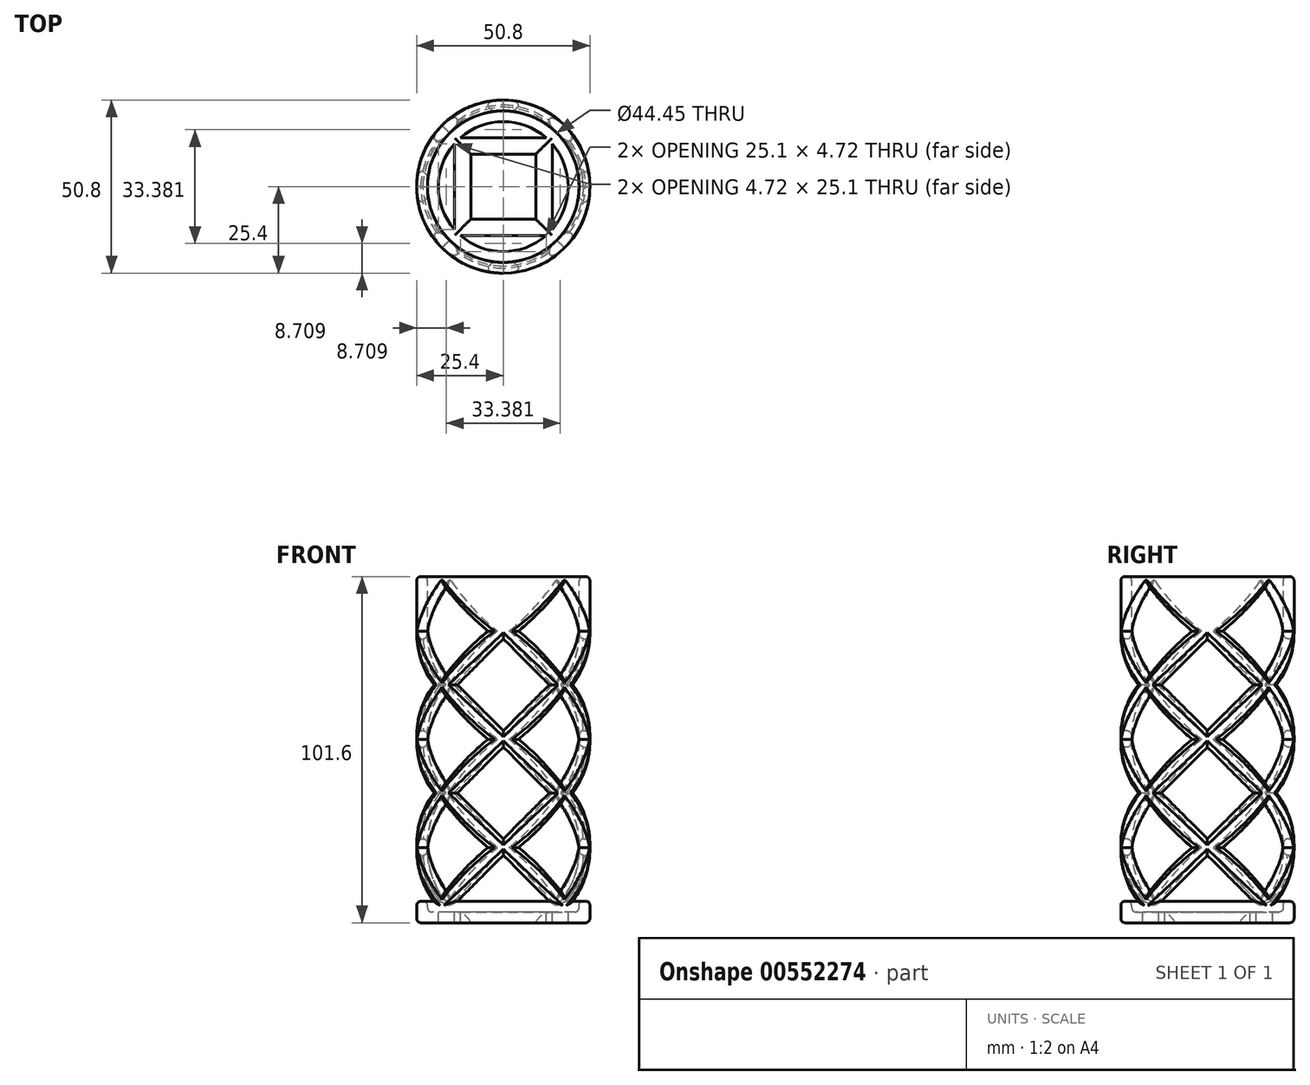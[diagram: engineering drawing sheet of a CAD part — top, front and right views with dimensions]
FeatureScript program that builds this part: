
annotation { "Feature Type Name" : "Feature", "Feature Type Description" : "" }
export const myFeature = defineFeature(function(context is Context, id is Id, definition is map)
    precondition{}
    {
        {
            var Q0;
            Q0=qCreatedBy(makeId("Top.planeOp"),FACE);
            var sketch = newSketch(context, id + "F0", { "sketchPlane" : qUnion([Q0])});
            skCircle(sketch, "E0", {"center": v(0, 0) * mm, "radius": 25.4 * mm});
            skSolve(sketch);
        }
        {
            var Q0;
            Q0=makeQuery(id+"F0.imprint","IMPRINT",FACE,{"disambiguationData":[TD([[makeQuery(id+"F0.imprint","IMPRINT",EDGE,{"derivedFrom":sQuery(id+"F0.wireOp",EDGE,"E0")}),1.0]])]});
            extrude(context, id + "F1", {"entities" : qUnion([Q0]), "depth" : 101.6 * mm, "offsetDistance" : 25.4 * mm});
        }
        {
            var Q0;
            Q0=qCreatedBy(makeId("Front.planeOp"),FACE);
            var sketch = newSketch(context, id + "F2", { "sketchPlane" : qUnion([Q0])});
            skLineSegment(sketch, "E1.0", {"start": v(-25.4, 0) * mm, "end": v(25.4, 0) * mm, "construction": true});
            skLineSegment(sketch, "E2", {"start": v(-25.4, 0) * mm, "end": v(-25.4, 101.6) * mm, "construction": true});
            skLineSegment(sketch, "E3.0", {"start": v(-25.4, 101.6) * mm, "end": v(25.4, 101.6) * mm, "construction": true});
            skLineSegment(sketch, "E4", {"start": v(25.4, 101.6) * mm, "end": v(25.4, 0) * mm, "construction": true});
            skLineSegment(sketch, "E5", {"start": v(0, 0) * mm, "end": v(0, 101.6) * mm, "construction": true});
            skCircle(sketch, "E6.cCircle", {"center": v(0, 133.35) * mm, "radius": 9.53 * mm, "construction": true});
            skLineSegment(sketch, "E6.0", {"start": v(0, 119.88) * mm, "end": v(-13.47, 133.35) * mm, "construction": true});
            skLineSegment(sketch, "E6.1", {"start": v(-13.47, 133.35) * mm, "end": v(0, 146.82) * mm, "construction": true});
            skLineSegment(sketch, "E6.2", {"start": v(0, 146.82) * mm, "end": v(13.47, 133.35) * mm, "construction": true});
            skLineSegment(sketch, "E6.3", {"start": v(13.47, 133.35) * mm, "end": v(0, 119.88) * mm, "construction": true});
            skLineSegment(sketch, "E7.0.1.0", {"start": v(0, 88.13) * mm, "end": v(-13.47, 101.6) * mm, "construction": true});
            skCircle(sketch, "E7.0.1.1", {"center": v(0, 101.6) * mm, "radius": 9.53 * mm, "construction": true});
            skLineSegment(sketch, "E7.0.1.2", {"start": v(-13.47, 101.6) * mm, "end": v(0, 115.07) * mm, "construction": true});
            skLineSegment(sketch, "E7.0.1.3", {"start": v(0, 115.07) * mm, "end": v(13.47, 101.6) * mm, "construction": true});
            skLineSegment(sketch, "E7.0.1.4", {"start": v(13.47, 101.6) * mm, "end": v(0, 88.13) * mm, "construction": true});
            skLineSegment(sketch, "E7.0.2.0", {"start": v(0, 56.38) * mm, "end": v(-13.47, 69.85) * mm});
            skCircle(sketch, "E7.0.2.1", {"center": v(0, 69.85) * mm, "radius": 9.53 * mm, "construction": true});
            skLineSegment(sketch, "E7.0.2.2", {"start": v(-13.47, 69.85) * mm, "end": v(0, 83.32) * mm});
            skLineSegment(sketch, "E7.0.2.3", {"start": v(0, 83.32) * mm, "end": v(13.47, 69.85) * mm});
            skLineSegment(sketch, "E7.0.2.4", {"start": v(13.47, 69.85) * mm, "end": v(0, 56.38) * mm});
            skLineSegment(sketch, "E7.0.3.0", {"start": v(0, 24.63) * mm, "end": v(-13.47, 38.1) * mm});
            skCircle(sketch, "E7.0.3.1", {"center": v(0, 38.1) * mm, "radius": 9.53 * mm, "construction": true});
            skLineSegment(sketch, "E7.0.3.2", {"start": v(-13.47, 38.1) * mm, "end": v(0, 51.57) * mm});
            skLineSegment(sketch, "E7.0.3.3", {"start": v(0, 51.57) * mm, "end": v(13.47, 38.1) * mm});
            skLineSegment(sketch, "E7.0.3.4", {"start": v(13.47, 38.1) * mm, "end": v(0, 24.63) * mm});
            skLineSegment(sketch, "E7.0.4.0", {"start": v(-6.74, -0.39) * mm, "end": v(-7.12, 0) * mm});
            skArc(sketch, "E7.0.4.1", {"start": v(-7.1, 0) * mm, "mid": v(-6.92, -0.2) * mm, "end": v(-6.74, -0.39) * mm, "construction": true});
            skLineSegment(sketch, "E7.0.4.2", {"start": v(-13.47, 6.35) * mm, "end": v(0, 19.82) * mm});
            skLineSegment(sketch, "E7.0.4.3", {"start": v(0, 19.82) * mm, "end": v(13.47, 6.35) * mm});
            skLineSegment(sketch, "E7.0.4.4", {"start": v(7.12, 0) * mm, "end": v(6.74, -0.39) * mm});
            skLineSegment(sketch, "E7.direction1", {"start": v(0, 119.88) * mm, "end": v(25.4, 119.88) * mm, "construction": true});
            skLineSegment(sketch, "E7.direction2", {"start": v(0, 119.88) * mm, "end": v(0, 88.13) * mm, "construction": true});
            skLineSegment(sketch, "E8", {"start": v(-13.47, 6.35) * mm, "end": v(13.47, 6.35) * mm});
            skArc(sketch, "E9.trimOffspring", {"start": v(6.74, -0.39) * mm, "mid": v(6.92, -0.2) * mm, "end": v(7.1, 0) * mm, "construction": true});
            skArc(sketch, "E10.trimOffspring", {"start": v(9.53, 6.35) * mm, "mid": v(0, 15.88) * mm, "end": v(-9.52, 6.35) * mm, "construction": true});
            skLineSegment(sketch, "E11", {"start": v(-25.4, 101.6) * mm, "end": v(0, 101.6) * mm, "construction": true});
            skLineSegment(sketch, "E12", {"start": v(25.4, 101.6) * mm, "end": v(0, 101.6) * mm, "construction": true});
            skSolve(sketch);
        }
        {
            var Q0;
            Q0=qSketchRegion(id+"F2",true);
            extrude(context, id + "F3", {"entities" : qUnion([Q0]), "operationType" : NewBodyOperationType.REMOVE, "endBound" : BoundingType.SYMMETRIC, "oppositeDirection" : true, "depth" : 50.8 * mm, "offsetDistance" : 25.4 * mm});
        }
        {
            var Q0;
            Q0=qCreatedBy(makeId("Right.planeOp"),FACE);
            var sketch = newSketch(context, id + "F4", { "sketchPlane" : qUnion([Q0])});
            skLineSegment(sketch, "E13.0", {"start": v(-25.4, 152.37) * mm, "end": v(25.4, 152.37) * mm, "construction": true});
            skLineSegment(sketch, "E14", {"start": v(0, -0.03) * mm, "end": v(0, 152.37) * mm, "construction": true});
            skLineSegment(sketch, "E15.0", {"start": v(-25.4, 152.4) * mm, "end": v(25.4, 152.4) * mm, "construction": true});
            skLineSegment(sketch, "E16", {"start": v(0, 0) * mm, "end": v(0, 152.4) * mm, "construction": true});
            skLineSegment(sketch, "E17", {"start": v(-25.4, 0) * mm, "end": v(-25.4, 152.4) * mm, "construction": true});
            skLineSegment(sketch, "E18", {"start": v(25.4, 152.4) * mm, "end": v(25.4, 0) * mm, "construction": true});
            skLineSegment(sketch, "E19", {"start": v(-25.4, 0) * mm, "end": v(25.4, 0) * mm, "construction": true});
            skCircle(sketch, "E20.cCircle", {"center": v(0, 133.35) * mm, "radius": 9.53 * mm, "construction": true});
            skLineSegment(sketch, "E20.0", {"start": v(0, 119.88) * mm, "end": v(-13.48, 133.35) * mm, "construction": true});
            skLineSegment(sketch, "E20.1", {"start": v(-13.48, 133.35) * mm, "end": v(0, 146.82) * mm, "construction": true});
            skLineSegment(sketch, "E20.2", {"start": v(0, 146.82) * mm, "end": v(13.46, 133.35) * mm, "construction": true});
            skLineSegment(sketch, "E20.3", {"start": v(13.46, 133.35) * mm, "end": v(0, 119.88) * mm, "construction": true});
            skLineSegment(sketch, "E21.0.1.0", {"start": v(0, 88.13) * mm, "end": v(-13.48, 101.6) * mm, "construction": true});
            skCircle(sketch, "E21.0.1.1", {"center": v(0, 101.6) * mm, "radius": 9.53 * mm, "construction": true});
            skLineSegment(sketch, "E21.0.1.2", {"start": v(-13.48, 101.6) * mm, "end": v(0, 115.07) * mm, "construction": true});
            skLineSegment(sketch, "E21.0.1.3", {"start": v(0, 115.07) * mm, "end": v(13.46, 101.6) * mm, "construction": true});
            skLineSegment(sketch, "E21.0.1.4", {"start": v(13.46, 101.6) * mm, "end": v(0, 88.13) * mm, "construction": true});
            skLineSegment(sketch, "E21.0.2.0", {"start": v(0, 56.38) * mm, "end": v(-13.48, 69.85) * mm});
            skCircle(sketch, "E21.0.2.1", {"center": v(0, 69.85) * mm, "radius": 9.53 * mm, "construction": true});
            skLineSegment(sketch, "E21.0.2.2", {"start": v(-13.48, 69.85) * mm, "end": v(0, 83.32) * mm});
            skLineSegment(sketch, "E21.0.2.3", {"start": v(0, 83.32) * mm, "end": v(13.46, 69.85) * mm});
            skLineSegment(sketch, "E21.0.2.4", {"start": v(13.46, 69.85) * mm, "end": v(0, 56.38) * mm});
            skLineSegment(sketch, "E21.0.3.0", {"start": v(0, 24.63) * mm, "end": v(-13.48, 38.1) * mm});
            skCircle(sketch, "E21.0.3.1", {"center": v(0, 38.1) * mm, "radius": 9.53 * mm, "construction": true});
            skLineSegment(sketch, "E21.0.3.2", {"start": v(-13.48, 38.1) * mm, "end": v(0, 51.57) * mm});
            skLineSegment(sketch, "E21.0.3.3", {"start": v(0, 51.57) * mm, "end": v(13.46, 38.1) * mm});
            skLineSegment(sketch, "E21.0.3.4", {"start": v(13.46, 38.1) * mm, "end": v(0, 24.63) * mm});
            skLineSegment(sketch, "E21.0.4.0", {"start": v(-6.74, -0.39) * mm, "end": v(-7.13, 0) * mm});
            skArc(sketch, "E21.0.4.1", {"start": v(-7.1, 0) * mm, "mid": v(-6.93, -0.2) * mm, "end": v(-6.74, -0.39) * mm, "construction": true});
            skLineSegment(sketch, "E21.0.4.2", {"start": v(-13.48, 6.35) * mm, "end": v(0, 19.82) * mm});
            skLineSegment(sketch, "E21.0.4.3", {"start": v(0, 19.82) * mm, "end": v(13.46, 6.35) * mm});
            skLineSegment(sketch, "E21.0.4.4", {"start": v(7.11, 0) * mm, "end": v(6.73, -0.39) * mm});
            skLineSegment(sketch, "E21.direction1", {"start": v(0, 119.88) * mm, "end": v(25.4, 119.88) * mm, "construction": true});
            skLineSegment(sketch, "E21.direction2", {"start": v(0, 119.88) * mm, "end": v(0, 88.13) * mm, "construction": true});
            skLineSegment(sketch, "E22", {"start": v(-13.48, 6.35) * mm, "end": v(13.46, 6.35) * mm});
            skArc(sketch, "E23.trimOffspring", {"start": v(6.73, -0.39) * mm, "mid": v(6.91, -0.2) * mm, "end": v(7.1, 0) * mm, "construction": true});
            skArc(sketch, "E24.trimOffspring", {"start": v(9.52, 6.35) * mm, "mid": v(0, 15.88) * mm, "end": v(-9.53, 6.35) * mm, "construction": true});
            skSolve(sketch);
        }
        {
            var Q0;
            Q0=qSketchRegion(id+"F4",true);
            var Q1;
            Q1=sQuery(id+"F4.wireOp",EDGE,"2f13abd6-07ff-4814-b25a-54ffae8c317d.5");
            var Q2;
            Q2=sQuery(id+"F4.wireOp",EDGE,"2f13abd6-07ff-4814-b25a-54ffae8c317d.4");
            var Q3;
            Q3=sQuery(id+"F4.wireOp",EDGE,"2f13abd6-07ff-4814-b25a-54ffae8c317d.0");
            var Q4;
            Q4=sQuery(id+"F4.wireOp",EDGE,"2f13abd6-07ff-4814-b25a-54ffae8c317d.3");
            var Q5;
            Q5=sQuery(id+"F4.wireOp",EDGE,"2f13abd6-07ff-4814-b25a-54ffae8c317d.2");
            var Q6;
            Q6=sQuery(id+"F4.wireOp",EDGE,"2f13abd6-07ff-4814-b25a-54ffae8c317d.1");
            var Q7;
            Q7=sQuery(id+"F4.wireOp",EDGE,"6f1e5377-79db-41f7-a9aa-e35f999cc832.0.1.7");
            var Q8;
            Q8=sQuery(id+"F4.wireOp",EDGE,"6f1e5377-79db-41f7-a9aa-e35f999cc832.0.1.4");
            var Q9;
            Q9=sQuery(id+"F4.wireOp",EDGE,"6f1e5377-79db-41f7-a9aa-e35f999cc832.0.1.1");
            var Q10;
            Q10=sQuery(id+"F4.wireOp",EDGE,"6f1e5377-79db-41f7-a9aa-e35f999cc832.0.1.2");
            var Q11;
            Q11=sQuery(id+"F4.wireOp",EDGE,"6f1e5377-79db-41f7-a9aa-e35f999cc832.0.1.0");
            var Q12;
            Q12=sQuery(id+"F4.wireOp",EDGE,"6f1e5377-79db-41f7-a9aa-e35f999cc832.0.1.6");
            var Q13;
            Q13=sQuery(id+"F4.wireOp",EDGE,"6f1e5377-79db-41f7-a9aa-e35f999cc832.0.2.2");
            var Q14;
            Q14=sQuery(id+"F4.wireOp",EDGE,"6f1e5377-79db-41f7-a9aa-e35f999cc832.0.2.1");
            var Q15;
            Q15=sQuery(id+"F4.wireOp",EDGE,"6f1e5377-79db-41f7-a9aa-e35f999cc832.0.2.4");
            var Q16;
            Q16=sQuery(id+"F4.wireOp",EDGE,"6f1e5377-79db-41f7-a9aa-e35f999cc832.0.2.7");
            var Q17;
            Q17=sQuery(id+"F4.wireOp",EDGE,"6f1e5377-79db-41f7-a9aa-e35f999cc832.0.2.6");
            var Q18;
            Q18=sQuery(id+"F4.wireOp",EDGE,"6f1e5377-79db-41f7-a9aa-e35f999cc832.0.2.0");
            var Q19;
            Q19=sQuery(id+"F4.wireOp",EDGE,"6f1e5377-79db-41f7-a9aa-e35f999cc832.0.3.4");
            var Q20;
            Q20=sQuery(id+"F4.wireOp",EDGE,"6f1e5377-79db-41f7-a9aa-e35f999cc832.0.3.2");
            var Q21;
            Q21=sQuery(id+"F4.wireOp",EDGE,"6f1e5377-79db-41f7-a9aa-e35f999cc832.0.3.1");
            var Q22;
            Q22=sQuery(id+"F4.wireOp",EDGE,"6f1e5377-79db-41f7-a9aa-e35f999cc832.0.3.7");
            var Q23;
            Q23=sQuery(id+"F4.wireOp",EDGE,"6f1e5377-79db-41f7-a9aa-e35f999cc832.0.3.6");
            var Q24;
            Q24=sQuery(id+"F4.wireOp",EDGE,"6f1e5377-79db-41f7-a9aa-e35f999cc832.0.3.0");
            var Q25;
            Q25=sQuery(id+"F4.wireOp",EDGE,"6f1e5377-79db-41f7-a9aa-e35f999cc832.0.4.4");
            var Q26;
            Q26=sQuery(id+"F4.wireOp",EDGE,"6f1e5377-79db-41f7-a9aa-e35f999cc832.0.4.1");
            var Q27;
            Q27=sQuery(id+"F4.wireOp",EDGE,"6f1e5377-79db-41f7-a9aa-e35f999cc832.0.4.2");
            var Q28;
            Q28=sQuery(id+"F4.wireOp",EDGE,"6f1e5377-79db-41f7-a9aa-e35f999cc832.0.4.0");
            var Q29;
            Q29=sQuery(id+"F4.wireOp",EDGE,"6f1e5377-79db-41f7-a9aa-e35f999cc832.0.4.6");
            var Q30;
            Q30=sQuery(id+"F4.wireOp",EDGE,"6f1e5377-79db-41f7-a9aa-e35f999cc832.0.4.7");
            var Q31;
            Q31=sQuery(id+"F4.wireOp",EDGE,"6f1e5377-79db-41f7-a9aa-e35f999cc832.0.5.4");
            var Q32;
            Q32=sQuery(id+"F4.wireOp",EDGE,"6f1e5377-79db-41f7-a9aa-e35f999cc832.0.5.7");
            var Q33;
            Q33=sQuery(id+"F4.wireOp",EDGE,"6f1e5377-79db-41f7-a9aa-e35f999cc832.0.5.6");
            var Q34;
            Q34=sQuery(id+"F4.wireOp",EDGE,"6f1e5377-79db-41f7-a9aa-e35f999cc832.0.5.0");
            var Q35;
            Q35=sQuery(id+"F4.wireOp",EDGE,"6f1e5377-79db-41f7-a9aa-e35f999cc832.0.5.2");
            var Q36;
            Q36=sQuery(id+"F4.wireOp",EDGE,"6f1e5377-79db-41f7-a9aa-e35f999cc832.0.5.1");
            extrude(context, id + "F5", {"entities" : qUnion([Q0]), "operationType" : NewBodyOperationType.REMOVE, "surfaceEntities" : qUnion([Q1, Q2, Q3, Q4, Q5, Q6, Q7, Q8, Q9, Q10, Q11, Q12, Q13, Q14, Q15, Q16, Q17, Q18, Q19, Q20, Q21, Q22, Q23, Q24, Q25, Q26, Q27, Q28, Q29, Q30, Q31, Q32, Q33, Q34, Q35, Q36]), "endBound" : BoundingType.SYMMETRIC, "oppositeDirection" : true, "depth" : 50.8 * mm, "offsetDistance" : 25.4 * mm});
        }
        {
            var Q0;
            Q0=makeQuery(id+"F1.opExtrude","SWEPT_FACE",FACE,{"disambiguationData":[OSD([sQuery(id+"F0.wireOp",EDGE,"E0")])]});
            cPlane(context, id + "F6", {"entities" : qUnion([Q0]), "cplaneType" : CPlaneType.LINE_ANGLE, "offset" : 25.4 * mm, "angle" : 45 * degree, "oppositeDirection" : true, "width" : 152.4 * mm, "height" : 152.4 * mm});
        }
        {
            var Q0;
            Q0=qCreatedBy(id+"F6.planeOp",FACE);
            var sketch = newSketch(context, id + "F7", { "sketchPlane" : qUnion([Q0])});
            skLineSegment(sketch, "E25.0", {"start": v(-25.4, 101.6) * mm, "end": v(25.4, 101.6) * mm, "construction": true});
            skLineSegment(sketch, "E26", {"start": v(25.4, 152.4) * mm, "end": v(25.4, 0) * mm, "construction": true});
            skLineSegment(sketch, "E27", {"start": v(-25.4, 0) * mm, "end": v(-25.4, 152.4) * mm, "construction": true});
            skLineSegment(sketch, "E28.0", {"start": v(-25.4, 0) * mm, "end": v(25.4, 0) * mm, "construction": true});
            skLineSegment(sketch, "E29", {"start": v(0, 0) * mm, "end": v(0, 101.6) * mm, "construction": true});
            skPoint(sketch, "E30.0", {"position": v(17.96, 88.14) * mm});
            skPoint(sketch, "E31.0", {"position": v(17.96, 83.31) * mm});
            skLineSegment(sketch, "E32", {"start": v(17.96, 83.31) * mm, "end": v(17.96, 88.14) * mm, "construction": true});
            skLineSegment(sketch, "E33", {"start": v(17.96, 85.72) * mm, "end": v(-25.4, 85.72) * mm, "construction": true});
            skCircle(sketch, "E34.cCircle", {"center": v(0, 117.35) * mm, "radius": 9.53 * mm, "construction": true});
            skLineSegment(sketch, "E34.0", {"start": v(0, 103.88) * mm, "end": v(-13.47, 117.35) * mm});
            skLineSegment(sketch, "E34.1", {"start": v(-13.47, 117.35) * mm, "end": v(0, 130.82) * mm});
            skLineSegment(sketch, "E34.2", {"start": v(0, 130.82) * mm, "end": v(13.47, 117.35) * mm});
            skLineSegment(sketch, "E34.3", {"start": v(13.47, 117.35) * mm, "end": v(0, 103.88) * mm});
            skLineSegment(sketch, "E35.0.1.0", {"start": v(0, 72.13) * mm, "end": v(-13.47, 85.6) * mm});
            skCircle(sketch, "E35.0.1.1", {"center": v(0, 85.6) * mm, "radius": 9.53 * mm, "construction": true});
            skLineSegment(sketch, "E35.0.1.2", {"start": v(-13.47, 85.6) * mm, "end": v(0, 99.07) * mm});
            skLineSegment(sketch, "E35.0.1.3", {"start": v(0, 99.07) * mm, "end": v(13.47, 85.6) * mm});
            skLineSegment(sketch, "E35.0.1.4", {"start": v(13.47, 85.6) * mm, "end": v(0, 72.13) * mm});
            skLineSegment(sketch, "E35.0.2.0", {"start": v(0, 40.38) * mm, "end": v(-13.47, 53.85) * mm});
            skCircle(sketch, "E35.0.2.1", {"center": v(0, 53.85) * mm, "radius": 9.53 * mm, "construction": true});
            skLineSegment(sketch, "E35.0.2.2", {"start": v(-13.47, 53.85) * mm, "end": v(0, 67.32) * mm});
            skLineSegment(sketch, "E35.0.2.3", {"start": v(0, 67.32) * mm, "end": v(13.47, 53.85) * mm});
            skLineSegment(sketch, "E35.0.2.4", {"start": v(13.47, 53.85) * mm, "end": v(0, 40.38) * mm});
            skLineSegment(sketch, "E35.0.3.0", {"start": v(0, 8.63) * mm, "end": v(-13.47, 22.1) * mm});
            skCircle(sketch, "E35.0.3.1", {"center": v(0, 22.1) * mm, "radius": 9.53 * mm, "construction": true});
            skLineSegment(sketch, "E35.0.3.2", {"start": v(-13.47, 22.1) * mm, "end": v(0, 35.57) * mm});
            skLineSegment(sketch, "E35.0.3.3", {"start": v(0, 35.57) * mm, "end": v(13.47, 22.1) * mm});
            skLineSegment(sketch, "E35.0.3.4", {"start": v(13.47, 22.1) * mm, "end": v(0, 8.63) * mm});
            skLineSegment(sketch, "E35.direction1", {"start": v(0, 103.88) * mm, "end": v(25.4, 103.88) * mm, "construction": true});
            skLineSegment(sketch, "E35.direction2", {"start": v(0, 103.88) * mm, "end": v(0, 72.13) * mm, "construction": true});
            skSolve(sketch);
        }
        {
            var Q0;
            Q0=qSketchRegion(id+"F7",true);
            extrude(context, id + "F8", {"entities" : qUnion([Q0]), "operationType" : NewBodyOperationType.REMOVE, "endBound" : BoundingType.SYMMETRIC, "oppositeDirection" : true, "depth" : 50.8 * mm, "offsetDistance" : 25.4 * mm});
        }
        {
            var Q0;
            Q0=makeQuery(id+"F1.opExtrude","SWEPT_FACE",FACE,{"disambiguationData":[OSD([sQuery(id+"F0.wireOp",EDGE,"E0")])]});
            cPlane(context, id + "F9", {"entities" : qUnion([Q0]), "cplaneType" : CPlaneType.LINE_ANGLE, "offset" : 25.4 * mm, "angle" : 45 * degree, "width" : 152.4 * mm, "height" : 152.4 * mm});
        }
        {
            var Q0;
            Q0=qCreatedBy(id+"F9.planeOp",FACE);
            var sketch = newSketch(context, id + "F10", { "sketchPlane" : qUnion([Q0])});
            skLineSegment(sketch, "E36.0", {"start": v(-25.4, 0) * mm, "end": v(25.4, 0) * mm, "construction": true});
            skLineSegment(sketch, "E37.0", {"start": v(-25.4, 101.6) * mm, "end": v(25.4, 101.6) * mm, "construction": true});
            skLineSegment(sketch, "E38", {"start": v(25.4, 152.4) * mm, "end": v(25.4, 0) * mm, "construction": true});
            skLineSegment(sketch, "E39", {"start": v(-25.4, 0) * mm, "end": v(-25.4, 152.4) * mm, "construction": true});
            skLineSegment(sketch, "E40", {"start": v(0, 0) * mm, "end": v(0, 101.6) * mm, "construction": true});
            skLineSegment(sketch, "E41.0", {"start": v(-25.4, 152.4) * mm, "end": v(25.4, 152.4) * mm, "construction": true});
            skLineSegment(sketch, "E42", {"start": v(0, 0) * mm, "end": v(0, 152.4) * mm, "construction": true});
            skPoint(sketch, "E43.0", {"position": v(17.96, 88.14) * mm});
            skPoint(sketch, "E44.0", {"position": v(17.96, 83.31) * mm});
            skLineSegment(sketch, "E45", {"start": v(17.96, 83.31) * mm, "end": v(17.96, 88.14) * mm, "construction": true});
            skLineSegment(sketch, "E46", {"start": v(17.96, 85.72) * mm, "end": v(-25.4, 85.72) * mm, "construction": true});
            skCircle(sketch, "E47.cCircle", {"center": v(0, 117.35) * mm, "radius": 9.53 * mm, "construction": true});
            skLineSegment(sketch, "E47.0", {"start": v(0, 103.88) * mm, "end": v(-13.47, 117.35) * mm});
            skLineSegment(sketch, "E47.1", {"start": v(-13.47, 117.35) * mm, "end": v(0, 130.82) * mm});
            skLineSegment(sketch, "E47.2", {"start": v(0, 130.82) * mm, "end": v(13.47, 117.35) * mm});
            skLineSegment(sketch, "E47.3", {"start": v(13.47, 117.35) * mm, "end": v(0, 103.88) * mm});
            skLineSegment(sketch, "E48.0.1.0", {"start": v(0, 72.13) * mm, "end": v(-13.47, 85.6) * mm});
            skCircle(sketch, "E48.0.1.1", {"center": v(0, 85.6) * mm, "radius": 9.53 * mm, "construction": true});
            skLineSegment(sketch, "E48.0.1.2", {"start": v(-13.47, 85.6) * mm, "end": v(0, 99.07) * mm});
            skLineSegment(sketch, "E48.0.1.3", {"start": v(0, 99.07) * mm, "end": v(13.47, 85.6) * mm});
            skLineSegment(sketch, "E48.0.1.4", {"start": v(13.47, 85.6) * mm, "end": v(0, 72.13) * mm});
            skLineSegment(sketch, "E48.0.2.0", {"start": v(0, 40.38) * mm, "end": v(-13.47, 53.85) * mm});
            skCircle(sketch, "E48.0.2.1", {"center": v(0, 53.85) * mm, "radius": 9.53 * mm, "construction": true});
            skLineSegment(sketch, "E48.0.2.2", {"start": v(-13.47, 53.85) * mm, "end": v(0, 67.32) * mm});
            skLineSegment(sketch, "E48.0.2.3", {"start": v(0, 67.32) * mm, "end": v(13.47, 53.85) * mm});
            skLineSegment(sketch, "E48.0.2.4", {"start": v(13.47, 53.85) * mm, "end": v(0, 40.38) * mm});
            skLineSegment(sketch, "E48.0.3.0", {"start": v(0, 8.63) * mm, "end": v(-13.47, 22.1) * mm});
            skCircle(sketch, "E48.0.3.1", {"center": v(0, 22.1) * mm, "radius": 9.53 * mm, "construction": true});
            skLineSegment(sketch, "E48.0.3.2", {"start": v(-13.47, 22.1) * mm, "end": v(0, 35.57) * mm});
            skLineSegment(sketch, "E48.0.3.3", {"start": v(0, 35.57) * mm, "end": v(13.47, 22.1) * mm});
            skLineSegment(sketch, "E48.0.3.4", {"start": v(13.47, 22.1) * mm, "end": v(0, 8.63) * mm});
            skLineSegment(sketch, "E48.direction1", {"start": v(0, 103.88) * mm, "end": v(25.4, 103.88) * mm, "construction": true});
            skLineSegment(sketch, "E48.direction2", {"start": v(0, 103.88) * mm, "end": v(0, 72.13) * mm, "construction": true});
            skSolve(sketch);
        }
        {
            var Q0;
            Q0=qSketchRegion(id+"F10",true);
            extrude(context, id + "F11", {"entities" : qUnion([Q0]), "operationType" : NewBodyOperationType.REMOVE, "endBound" : BoundingType.SYMMETRIC, "oppositeDirection" : true, "depth" : 50.8 * mm, "offsetDistance" : 25.4 * mm});
        }
        {
            var Q0;
            Q0=makeQuery(id+"F1.opExtrude","CAP_FACE",FACE,{"disambiguationData":[OSD([sQuery(id+"F0.wireOp",EDGE,"E0")])],"isStart":false});
            var sketch = newSketch(context, id + "F12", { "sketchPlane" : qUnion([Q0])});
            skCircle(sketch, "E49", {"center": v(0, 0) * mm, "radius": 22.23 * mm});
            skCircle(sketch, "E50.cCircle", {"center": v(0, 0) * mm, "radius": 9.53 * mm, "construction": true});
            skLineSegment(sketch, "E50.0", {"start": v(9.52, -9.53) * mm, "end": v(-9.52, -9.53) * mm});
            skLineSegment(sketch, "E50.1", {"start": v(-9.52, -9.53) * mm, "end": v(-9.53, 9.53) * mm});
            skLineSegment(sketch, "E50.2", {"start": v(-9.53, 9.53) * mm, "end": v(9.53, 9.53) * mm});
            skLineSegment(sketch, "E50.3", {"start": v(9.53, 9.52) * mm, "end": v(9.53, -9.53) * mm});
            skPoint(sketch, "E50.0.midPoint", {"position": v(0, -9.53) * mm});
            skCircle(sketch, "E51", {"center": v(0, 0) * mm, "radius": 19.05 * mm});
            skLineSegment(sketch, "E52", {"start": v(-14.33, 12.55) * mm, "end": v(-14.33, -12.55) * mm});
            skLineSegment(sketch, "E53", {"start": v(-12.55, -14.33) * mm, "end": v(12.55, -14.33) * mm});
            skLineSegment(sketch, "E54", {"start": v(14.33, -12.55) * mm, "end": v(14.33, 12.55) * mm});
            skLineSegment(sketch, "E55", {"start": v(12.55, 14.33) * mm, "end": v(-12.55, 14.33) * mm});
            skSolve(sketch);
        }
        {
            var Q0;
            Q0=makeQuery(id+"F12.imprint","IMPRINT",FACE,{"disambiguationData":[TD([[makeQuery(id+"F12.imprint","IMPRINT",EDGE,{"derivedFrom":sQuery(id+"F12.wireOp",EDGE,"E50.0")}),-1.0]])]});
            var Q1;
            {var subQ0=sQuery(id+"F12.wireOp",EDGE,"6df1d413-d965-45c5-9bc1-fe74c4bacd03.1.5");Q1=makeQuery(id+"F12.imprint","IMPRINT",FACE,{"disambiguationData":[TD([[makeQuery(id+"F12.imprint","IMPRINT",EDGE,{"derivedFrom":subQ0}),-1.0]])]});}
            var Q2;
            {var subQ0=sQuery(id+"F12.wireOp",EDGE,"6df1d413-d965-45c5-9bc1-fe74c4bacd03.1.5");Q2=makeQuery(id+"F12.imprint","IMPRINT",FACE,{"disambiguationData":[TD([[makeQuery(id+"F12.imprint","IMPRINT",EDGE,{"derivedFrom":subQ0}),-1.0]])]});}
            var Q3;
            {var subQ0=sQuery(id+"F12.wireOp",EDGE,"1db86502-511d-4738-918a-1fb412958f63.1.0.2");Q3=makeQuery(id+"F12.imprint","IMPRINT",FACE,{"disambiguationData":[TD([[makeQuery(id+"F12.imprint","IMPRINT",EDGE,{"derivedFrom":subQ0}),-1.0]])]});}
            var Q4;
            {var subQ0=sQuery(id+"F12.wireOp",EDGE,"6df1d413-d965-45c5-9bc1-fe74c4bacd03.3.5");Q4=makeQuery(id+"F12.imprint","IMPRINT",FACE,{"disambiguationData":[TD([[makeQuery(id+"F12.imprint","IMPRINT",EDGE,{"derivedFrom":subQ0}),-1.0]])]});}
            var Q5;
            {var subQ0=sQuery(id+"F12.wireOp",EDGE,"6df1d413-d965-45c5-9bc1-fe74c4bacd03.2.5");Q5=makeQuery(id+"F12.imprint","IMPRINT",FACE,{"disambiguationData":[TD([[makeQuery(id+"F12.imprint","IMPRINT",EDGE,{"derivedFrom":subQ0}),-1.0]])]});}
            var Q6;
            {var subQ0=sQuery(id+"F12.wireOp",EDGE,"RcPyOSS5-Rkkl-329T-9cvf-4NeGbcBbp6hW.bottom");Q6=makeQuery(id+"F12.imprint","IMPRINT",FACE,{"disambiguationData":[TD([[makeQuery(id+"F12.imprint","IMPRINT",EDGE,{"derivedFrom":subQ0}),-1.0]])]});}
            var Q7;
            {var subQ0=sQuery(id+"F12.wireOp",EDGE,"RcPyOSS5-Rkkl-329T-9cvf-4NeGbcBbp6hW.right");Q7=makeQuery(id+"F12.imprint","IMPRINT",FACE,{"disambiguationData":[TD([[makeQuery(id+"F12.imprint","IMPRINT",EDGE,{"derivedFrom":subQ0}),-1.0]])]});}
            var Q8;
            {var subQ0=sQuery(id+"F12.wireOp",EDGE,"RcPyOSS5-Rkkl-329T-9cvf-4NeGbcBbp6hW.left");Q8=makeQuery(id+"F12.imprint","IMPRINT",FACE,{"disambiguationData":[TD([[makeQuery(id+"F12.imprint","IMPRINT",EDGE,{"derivedFrom":subQ0}),1.0]])]});}
            var Q9;
            {var subQ0=sQuery(id+"F12.wireOp",EDGE,"RcPyOSS5-Rkkl-329T-9cvf-4NeGbcBbp6hW.top");Q9=makeQuery(id+"F12.imprint","IMPRINT",FACE,{"disambiguationData":[TD([[makeQuery(id+"F12.imprint","IMPRINT",EDGE,{"derivedFrom":subQ0}),1.0]])]});}
            var Q10;
            {var subQ0=sQuery(id+"F12.wireOp",EDGE,"E52");Q10=makeQuery(id+"F12.imprint","IMPRINT",FACE,{"disambiguationData":[TD([[makeQuery(id+"F12.imprint","IMPRINT",EDGE,{"derivedFrom":subQ0}),-1.0]])]});}
            var Q11;
            {var subQ0=sQuery(id+"F12.wireOp",EDGE,"E55");Q11=makeQuery(id+"F12.imprint","IMPRINT",FACE,{"disambiguationData":[TD([[makeQuery(id+"F12.imprint","IMPRINT",EDGE,{"derivedFrom":subQ0}),-1.0]])]});}
            var Q12;
            {var subQ0=sQuery(id+"F12.wireOp",EDGE,"E54");Q12=makeQuery(id+"F12.imprint","IMPRINT",FACE,{"disambiguationData":[TD([[makeQuery(id+"F12.imprint","IMPRINT",EDGE,{"derivedFrom":subQ0}),-1.0]])]});}
            var Q13;
            {var subQ0=sQuery(id+"F12.wireOp",EDGE,"E53");Q13=makeQuery(id+"F12.imprint","IMPRINT",FACE,{"disambiguationData":[TD([[makeQuery(id+"F12.imprint","IMPRINT",EDGE,{"derivedFrom":subQ0}),-1.0]])]});}
            var Q14;
            Q14=makeQuery(id+"F12.imprint","IMPRINT",FACE,{"disambiguationData":[TD([[makeQuery(id+"F12.imprint","IMPRINT",EDGE,{"derivedFrom":sQuery(id+"F12.wireOp",EDGE,"E50.0")}),1.0]])]});
            var Q15;
            Q15=makeQuery(id+"F12.imprint","IMPRINT",FACE,{"disambiguationData":[TD([[makeQuery(id+"F12.imprint","IMPRINT",EDGE,{"derivedFrom":sQuery(id+"F12.wireOp",EDGE,"E49")}),1.0]])]});
            extrude(context, id + "F13", {"entities" : qUnion([Q0, Q1, Q2, Q3, Q4, Q5, Q6, Q7, Q8, Q9, Q10, Q11, Q12, Q13, Q14, Q15]), "operationType" : NewBodyOperationType.REMOVE, "oppositeDirection" : true, "depth" : 98.45 * mm, "offsetDistance" : 25.4 * mm});
        }
        {
            var Q0;
            {var subQ0=sQuery(id+"F12.wireOp",EDGE,"6df1d413-d965-45c5-9bc1-fe74c4bacd03.2.5");Q0=makeQuery(id+"F12.imprint","IMPRINT",FACE,{"disambiguationData":[TD([[makeQuery(id+"F12.imprint","IMPRINT",EDGE,{"derivedFrom":subQ0}),-1.0]])]});}
            var Q1;
            Q1=makeQuery(id+"F12.imprint","IMPRINT",FACE,{"disambiguationData":[TD([[makeQuery(id+"F12.imprint","IMPRINT",EDGE,{"derivedFrom":sQuery(id+"F12.wireOp",EDGE,"E50.0")}),-1.0]])]});
            var Q2;
            {var subQ0=sQuery(id+"F12.wireOp",EDGE,"6df1d413-d965-45c5-9bc1-fe74c4bacd03.1.5");Q2=makeQuery(id+"F12.imprint","IMPRINT",FACE,{"disambiguationData":[TD([[makeQuery(id+"F12.imprint","IMPRINT",EDGE,{"derivedFrom":subQ0}),-1.0]])]});}
            var Q3;
            {var subQ0=sQuery(id+"F12.wireOp",EDGE,"1db86502-511d-4738-918a-1fb412958f63.1.0.2");Q3=makeQuery(id+"F12.imprint","IMPRINT",FACE,{"disambiguationData":[TD([[makeQuery(id+"F12.imprint","IMPRINT",EDGE,{"derivedFrom":subQ0}),-1.0]])]});}
            var Q4;
            {var subQ0=sQuery(id+"F12.wireOp",EDGE,"6df1d413-d965-45c5-9bc1-fe74c4bacd03.3.5");Q4=makeQuery(id+"F12.imprint","IMPRINT",FACE,{"disambiguationData":[TD([[makeQuery(id+"F12.imprint","IMPRINT",EDGE,{"derivedFrom":subQ0}),-1.0]])]});}
            var Q5;
            {var subQ0=sQuery(id+"F12.wireOp",EDGE,"RcPyOSS5-Rkkl-329T-9cvf-4NeGbcBbp6hW.bottom");Q5=makeQuery(id+"F12.imprint","IMPRINT",FACE,{"disambiguationData":[TD([[makeQuery(id+"F12.imprint","IMPRINT",EDGE,{"derivedFrom":subQ0}),-1.0]])]});}
            var Q6;
            {var subQ0=sQuery(id+"F12.wireOp",EDGE,"RcPyOSS5-Rkkl-329T-9cvf-4NeGbcBbp6hW.right");Q6=makeQuery(id+"F12.imprint","IMPRINT",FACE,{"disambiguationData":[TD([[makeQuery(id+"F12.imprint","IMPRINT",EDGE,{"derivedFrom":subQ0}),-1.0]])]});}
            var Q7;
            {var subQ0=sQuery(id+"F12.wireOp",EDGE,"RcPyOSS5-Rkkl-329T-9cvf-4NeGbcBbp6hW.left");Q7=makeQuery(id+"F12.imprint","IMPRINT",FACE,{"disambiguationData":[TD([[makeQuery(id+"F12.imprint","IMPRINT",EDGE,{"derivedFrom":subQ0}),1.0]])]});}
            var Q8;
            {var subQ0=sQuery(id+"F12.wireOp",EDGE,"RcPyOSS5-Rkkl-329T-9cvf-4NeGbcBbp6hW.top");Q8=makeQuery(id+"F12.imprint","IMPRINT",FACE,{"disambiguationData":[TD([[makeQuery(id+"F12.imprint","IMPRINT",EDGE,{"derivedFrom":subQ0}),1.0]])]});}
            var Q9;
            {var subQ0=sQuery(id+"F12.wireOp",EDGE,"E52");Q9=makeQuery(id+"F12.imprint","IMPRINT",FACE,{"disambiguationData":[TD([[makeQuery(id+"F12.imprint","IMPRINT",EDGE,{"derivedFrom":subQ0}),-1.0]])]});}
            var Q10;
            {var subQ0=sQuery(id+"F12.wireOp",EDGE,"E55");Q10=makeQuery(id+"F12.imprint","IMPRINT",FACE,{"disambiguationData":[TD([[makeQuery(id+"F12.imprint","IMPRINT",EDGE,{"derivedFrom":subQ0}),-1.0]])]});}
            var Q11;
            {var subQ0=sQuery(id+"F12.wireOp",EDGE,"E54");Q11=makeQuery(id+"F12.imprint","IMPRINT",FACE,{"disambiguationData":[TD([[makeQuery(id+"F12.imprint","IMPRINT",EDGE,{"derivedFrom":subQ0}),-1.0]])]});}
            var Q12;
            {var subQ0=sQuery(id+"F12.wireOp",EDGE,"E53");Q12=makeQuery(id+"F12.imprint","IMPRINT",FACE,{"disambiguationData":[TD([[makeQuery(id+"F12.imprint","IMPRINT",EDGE,{"derivedFrom":subQ0}),-1.0]])]});}
            extrude(context, id + "F14", {"entities" : qUnion([Q0, Q1, Q2, Q3, Q4, Q5, Q6, Q7, Q8, Q9, Q10, Q11, Q12]), "operationType" : NewBodyOperationType.REMOVE, "endBound" : BoundingType.THROUGH_ALL, "oppositeDirection" : true, "depth" : 25.4 * mm, "offsetDistance" : 25.4 * mm});
        }
        {
            var Q0;
            Q0=makeQuery(id+"F14.boolean.opBoolean","INTERSECT",EDGE,{"derivedFrom":[makeQuery(id+"F13.boolean.opBoolean","COPY",FACE,{"derivedFrom":makeQuery(id+"F13.opExtrude","CAP_FACE",FACE,{"disambiguationData":[OSD([sQuery(id+"F12.wireOp",EDGE,"E49")])],"isStart":false})}),makeQuery(id+"F14.opExtrude","SWEPT_FACE",FACE,{"disambiguationData":[OSD([sQuery(id+"F12.wireOp",EDGE,"E50.2")])]})]});
            var Q1;
            Q1=makeQuery(id+"F14.boolean.opBoolean","INTERSECT",EDGE,{"derivedFrom":[makeQuery(id+"F13.boolean.opBoolean","COPY",FACE,{"derivedFrom":makeQuery(id+"F13.opExtrude","CAP_FACE",FACE,{"disambiguationData":[OSD([sQuery(id+"F12.wireOp",EDGE,"E49")])],"isStart":false})}),makeQuery(id+"F14.opExtrude","SWEPT_FACE",FACE,{"disambiguationData":[OSD([sQuery(id+"F12.wireOp",EDGE,"E50.1")])]})]});
            var Q2;
            Q2=makeQuery(id+"F14.boolean.opBoolean","INTERSECT",EDGE,{"derivedFrom":[makeQuery(id+"F13.boolean.opBoolean","COPY",FACE,{"derivedFrom":makeQuery(id+"F13.opExtrude","CAP_FACE",FACE,{"disambiguationData":[OSD([sQuery(id+"F12.wireOp",EDGE,"E49")])],"isStart":false})}),makeQuery(id+"F14.opExtrude","SWEPT_FACE",FACE,{"disambiguationData":[OSD([sQuery(id+"F12.wireOp",EDGE,"E50.3")])]})]});
            var Q3;
            Q3=makeQuery(id+"F14.boolean.opBoolean","INTERSECT",EDGE,{"derivedFrom":[makeQuery(id+"F13.boolean.opBoolean","COPY",FACE,{"derivedFrom":makeQuery(id+"F13.opExtrude","CAP_FACE",FACE,{"disambiguationData":[OSD([sQuery(id+"F12.wireOp",EDGE,"E49")])],"isStart":false})}),makeQuery(id+"F14.opExtrude","SWEPT_FACE",FACE,{"disambiguationData":[OSD([sQuery(id+"F12.wireOp",EDGE,"E50.0")])]})]});
            fillet(context, id + "F15", {"entities" : qUnion([Q0, Q1, Q2, Q3]), "radius" : 5.08 * mm, "tangentPropagation" : true, "allowEdgeOverflow" : false});
        }
        {
            var Q0;
            {var subQ0=makeQuery(id+"F13.boolean.opBoolean","COPY",FACE,{"derivedFrom":makeQuery(id+"F13.opExtrude","CAP_FACE",FACE,{"disambiguationData":[OSD([sQuery(id+"F12.wireOp",EDGE,"E49")])],"isStart":false})});Q0=makeQuery(id+"F15.opFillet","BLEND_EDGE",EDGE,{"blendedFrom":[makeQuery(id+"F14.boolean.opBoolean","INTERSECT",EDGE,{"derivedFrom":[subQ0,makeQuery(id+"F14.opExtrude","SWEPT_FACE",FACE,{"disambiguationData":[OSD([sQuery(id+"F12.wireOp",EDGE,"E50.1")])]})]}),subQ0],"blendedInto":[subQ0]});}
            var Q1;
            {var subQ0=makeQuery(id+"F13.boolean.opBoolean","COPY",FACE,{"derivedFrom":makeQuery(id+"F13.opExtrude","CAP_FACE",FACE,{"disambiguationData":[OSD([sQuery(id+"F12.wireOp",EDGE,"E49")])],"isStart":false})});Q1=makeQuery(id+"F15.opFillet","BLEND_EDGE",EDGE,{"blendedFrom":[makeQuery(id+"F14.boolean.opBoolean","INTERSECT",EDGE,{"derivedFrom":[subQ0,makeQuery(id+"F14.opExtrude","SWEPT_FACE",FACE,{"disambiguationData":[OSD([sQuery(id+"F12.wireOp",EDGE,"E50.2")])]})]}),subQ0],"blendedInto":[subQ0]});}
            var Q2;
            {var subQ0=makeQuery(id+"F13.boolean.opBoolean","COPY",FACE,{"derivedFrom":makeQuery(id+"F13.opExtrude","CAP_FACE",FACE,{"disambiguationData":[OSD([sQuery(id+"F12.wireOp",EDGE,"E49")])],"isStart":false})});Q2=makeQuery(id+"F15.opFillet","BLEND_EDGE",EDGE,{"blendedFrom":[makeQuery(id+"F14.boolean.opBoolean","INTERSECT",EDGE,{"derivedFrom":[subQ0,makeQuery(id+"F14.opExtrude","SWEPT_FACE",FACE,{"disambiguationData":[OSD([sQuery(id+"F12.wireOp",EDGE,"E50.3")])]})]}),subQ0],"blendedInto":[subQ0]});}
            var Q3;
            Q3=makeQuery(id+"F1.opExtrude","SWEPT_FACE",FACE,{"disambiguationData":[OSD([sQuery(id+"F0.wireOp",EDGE,"E0")])]});
            var Q4;
            Q4=makeQuery(id+"F13.boolean.opBoolean","COPY",FACE,{"derivedFrom":makeQuery(id+"F13.opExtrude","SWEPT_FACE",FACE,{"disambiguationData":[OSD([sQuery(id+"F12.wireOp",EDGE,"E49")])]})});
            fillet(context, id + "F16", {"entities" : qUnion([Q0, Q1, Q2, Q3, Q4]), "radius" : 1.27 * mm, "tangentPropagation" : true, "allowEdgeOverflow" : false});
        }
    });
